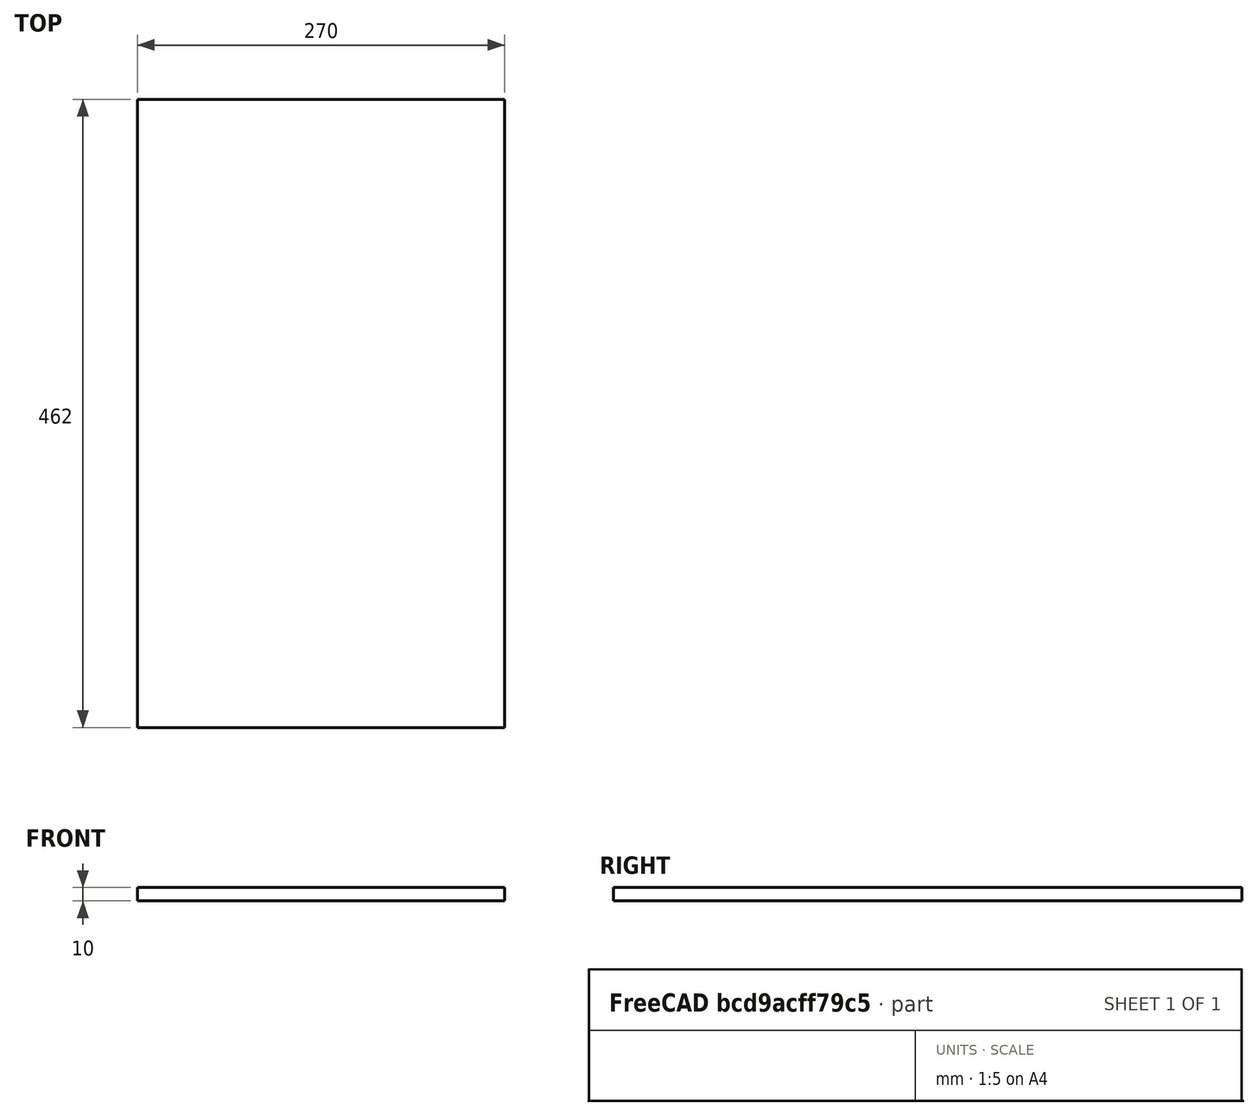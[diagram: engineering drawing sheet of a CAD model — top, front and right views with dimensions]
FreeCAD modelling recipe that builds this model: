
FCSTD DOCUMENT  (FreeCAD 0.18R16131 (Git))
Label: 500_Pedastil_Mid_Floor
License: All rights reserved
LicenseURL: http://en.wikipedia.org/wiki/All_rights_reserved
objects: Sketcher::SketchObject×2, PartDesign::Pad×1, Spreadsheet::Sheet×1, PartDesign::Body×1, App::Part×1
note: 5 computed .brp shape members not serialized (recipe doc carries the construction recipe); baked Part::Feature solids carry a one-line shape summary decoded from their .brp

FEATURE [Sketcher::SketchObject] Sketch
  MapMode = 5
  Support = -> [XY_Plane001]
  expr: Constraints[6] = Spreadsheet.Width
  expr: Constraints[5] = Spreadsheet.Depth
  sketch-geometry (7):
    g0: LineSegment StartX=0 StartY=413.879 StartZ=0 EndX=0 EndY=462 EndZ=0
    g1: LineSegment StartX=0 StartY=462 StartZ=0 EndX=270 EndY=462 EndZ=0
    g2: LineSegment StartX=270 StartY=462 StartZ=0 EndX=270 EndY=0 EndZ=0
    g3: LineSegment StartX=270 StartY=0 StartZ=0 EndX=0 EndY=0 EndZ=0
    g4: LineSegment StartX=0 StartY=0 StartZ=0 EndX=0 EndY=413.879 EndZ=0
    g5: LineSegment [constr] StartX=0 StartY=0 StartZ=0 EndX=135 EndY=231 EndZ=0
    g6: LineSegment [constr] StartX=135 StartY=231 StartZ=0 EndX=270 EndY=462 EndZ=0
  constraints (18):
    c: Coincident(g1,g0)
    c: Horizontal(g1)
    c: Horizontal(g3)
    c: Coincident(g4,g3)
    c: Coincident(g3,g2)
    c: Distance(g1) = 270
    c: DistanceY(g2,g2) = 462
    c: Coincident(g1,g2)
    c: Coincident(g5,g3)
    c: Coincident(g6,g1)
    c: Equal(g6,g5)
    c: Coincident(g5,g6)
    c: Parallel(g5,g6)
    c: Vertical(g0)
    c: Vertical(g2)
    c: Coincident(g4,g0)
    c: Vertical(g4)
    c: Coincident(g3,g-1)
FEATURE [PartDesign::Pad] Pad
  Length = 10
  Length2 = 100
  Profile = -> Sketch
  Reversed = true
  Type = 0
  expr: Length = Spreadsheet.T
FEATURE [Spreadsheet::Sheet] Spreadsheet
  cells = B2=Dependancies; C2=Value; D2=Nominal; E2=Var; F2=Description; G2=FILE; B3=Side Wall pedistil; C3=19; B4=Sidewall Width; C4==+415 - 100; D4=415; B5=Front Wall thickness; C5=10; B8=BODY FLOOR; C8=Value; D8=Nominal; E8=Var; F8=Description; G8=FILE; B9=Orientation; C9=(0,0,1); F9=XY; B10=Z=; C10(T)=10; E10=.T; F10=Thichness Z; B11=Y=; C11(Width)==500 - 2 * C3; D11=500; E11=.W; F11=Width Y; B12=X=; C12(Depth)==D12 - 4 * C5 - 5; D12==+C4; E12=.D; F12=Depth X
FEATURE [Sketcher::SketchObject] Sketch001
  MapMode = 5
  Placement = pos=(0,0,-10) rot=(1,0,0;3.14159rad)
  Support = -> [Pad]
  sketch-geometry (3):
    g0: LineSegment StartX=16.778 StartY=-210.88 StartZ=0 EndX=17.2836 EndY=-236.816 EndZ=0
    g1: LineSegment StartX=17.2836 StartY=-236.816 StartZ=0 EndX=84.9762 EndY=-236.816 EndZ=0
    g2: LineSegment StartX=84.9762 StartY=-236.816 StartZ=0 EndX=16.778 EndY=-210.88 EndZ=0
  constraints (4):
    c: Coincident(g0,g1)
    c: Horizontal(g1)
    c: Coincident(g1,g2)
    c: Coincident(g2,g0)
FEATURE [PartDesign::Body] PadBody
  Group = -> [Sketch,Pad]
  Origin = -> Origin001
  Tip = -> Pad
FEATURE [App::Part] Part
  Group = -> [PadBody]
  License = CC BY 3.0
  LicenseURL = http://creativecommons.org/licenses/by/3.0/
  Origin = -> Origin
